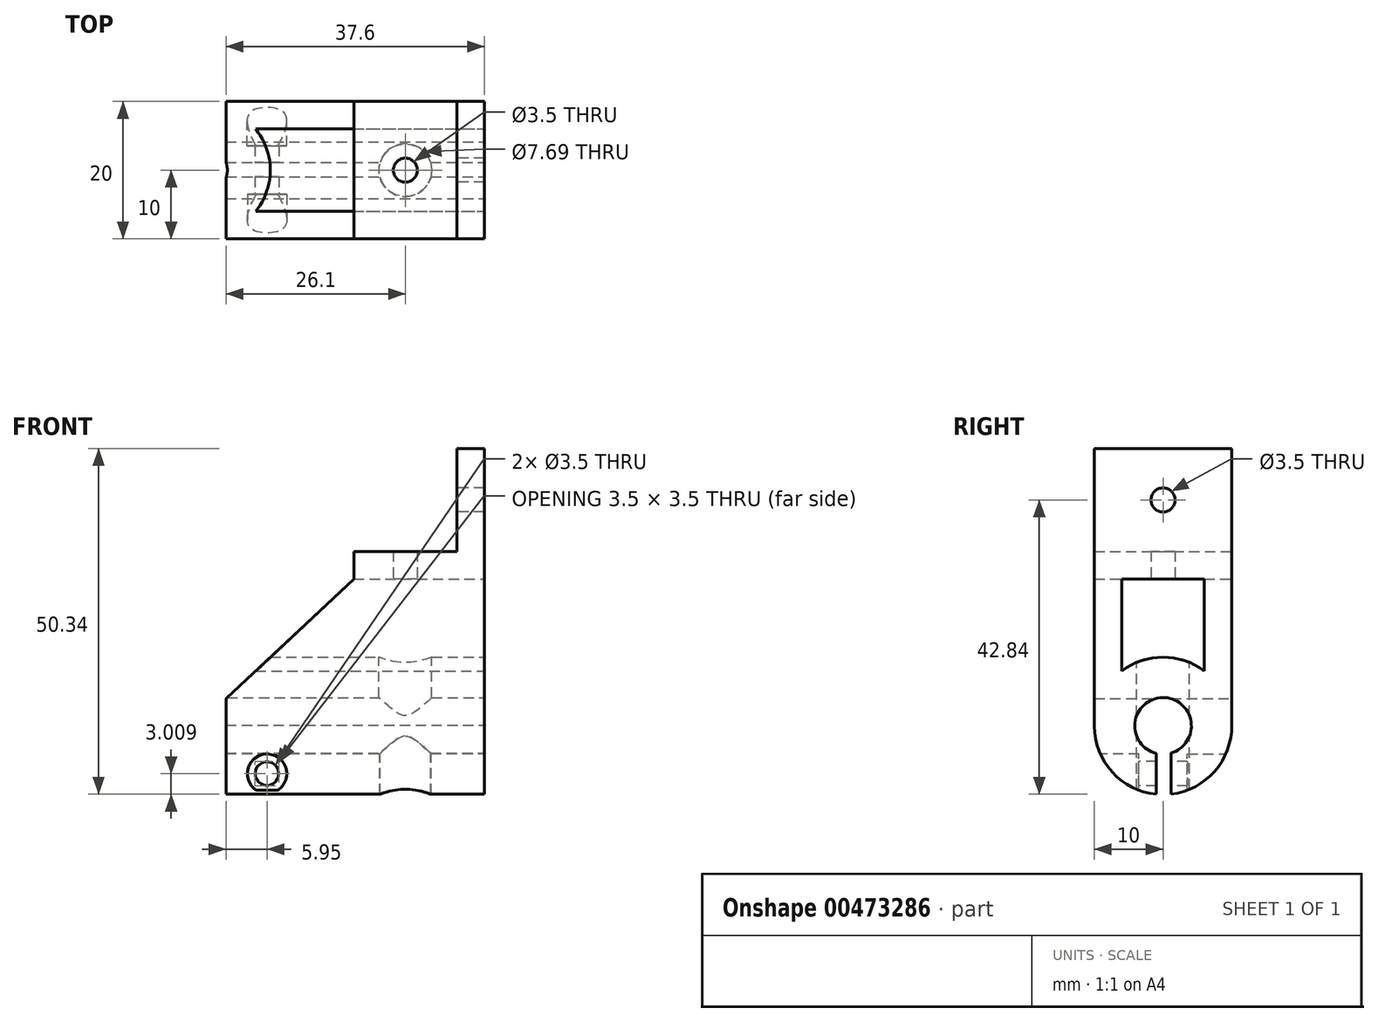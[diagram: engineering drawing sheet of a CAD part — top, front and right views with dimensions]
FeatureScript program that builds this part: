
annotation { "Feature Type Name" : "Feature", "Feature Type Description" : "" }
export const myFeature = defineFeature(function(context is Context, id is Id, definition is map)
    precondition{}
    {
        {
            var Q0;
            Q0=qCreatedBy(makeId("Top.planeOp"),FACE);
            var sketch = newSketch(context, id + "F0", { "sketchPlane" : qUnion([Q0])});
            skLineSegment(sketch, "E0.bottom", {"start": v(0, 0) * mm, "end": v(-19, 0) * mm});
            skLineSegment(sketch, "E0.top", {"start": v(0, 20) * mm, "end": v(-19, 20) * mm});
            skLineSegment(sketch, "E0.left", {"start": v(0, 0) * mm, "end": v(0, 20) * mm});
            skLineSegment(sketch, "E0.right", {"start": v(-19, 0) * mm, "end": v(-19, 20) * mm});
            skPoint(sketch, "E1.centerSnap0", {"position": v(-9.5, 20) * mm});
            skPoint(sketch, "E1.centerSnap1", {"position": v(-19, 10) * mm});
            skCircle(sketch, "E2", {"center": v(-11.5, 10) * mm, "radius": 1.75 * mm});
            skSolve(sketch);
        }
        {
            var Q0;
            Q0 = qSketchRegion(id + "F0", true);
            extrude(context, id + "F1", {"entities" : qUnion([Q0]), "depth" : 4 * mm, "offsetDistance" : 25 * mm});
        }
        {
            var Q0;
            Q0=makeQuery(id+"F1.opExtrude","CAP_FACE",FACE,{"disambiguationData":[OSD([sQuery(id+"F0.wireOp",EDGE,"E0.bottom"),sQuery(id+"F0.wireOp",EDGE,"E0.top"),sQuery(id+"F0.wireOp",EDGE,"E0.left"),sQuery(id+"F0.wireOp",EDGE,"E0.right"),sQuery(id+"F0.wireOp",EDGE,"E1")])],"isStart":false});
            var sketch = newSketch(context, id + "F2", { "sketchPlane" : qUnion([Q0])});
            skSolve(sketch);
        }
        {
            var Q0;
            Q0=makeQuery(id+"F2.imprint","IMPRINT",FACE,{"disambiguationData":[TD([[makeQuery(id+"F2.imprint","IMPRINT",EDGE,{"derivedFrom":makeQuery(id+"F1.opExtrude","CAP_EDGE",EDGE,{"disambiguationData":[OSD([sQuery(id+"F0.wireOp",EDGE,"E0.bottom")])],"isStart":false})}),-1.0]])]});
            var sketch = newSketch(context, id + "F3", { "sketchPlane" : qUnion([Q0])});
            skPoint(sketch, "E3.0", {"position": v(0, 20) * mm});
            skLineSegment(sketch, "E4.bottom", {"start": v(0, 0) * mm, "end": v(-4, 0) * mm});
            skLineSegment(sketch, "E4.top", {"start": v(0, 20) * mm, "end": v(-4, 20) * mm});
            skLineSegment(sketch, "E4.left", {"start": v(0, 0) * mm, "end": v(0, 20) * mm});
            skLineSegment(sketch, "E4.right", {"start": v(-4, 0) * mm, "end": v(-4, 20) * mm});
            skSolve(sketch);
        }
        {
            var Q0;
            Q0 = qSketchRegion(id + "F3", true);
            extrude(context, id + "F4", {"entities" : qUnion([Q0]), "operationType" : NewBodyOperationType.ADD, "depth" : 15 * mm, "offsetDistance" : 25 * mm});
        }
        {
            var Q0;
            Q0=makeQuery(id+"F4.opExtrude","SWEPT_FACE",FACE,{"disambiguationData":[OSD([sQuery(id+"F3.wireOp",EDGE,"E4.right")])]});
            var sketch = newSketch(context, id + "F5", { "sketchPlane" : qUnion([Q0])});
            skCircle(sketch, "E5", {"center": v(-10, 11.5) * mm, "radius": 1.75 * mm});
            skPoint(sketch, "E5.centerSnap0", {"position": v(-20, 11.5) * mm});
            skPoint(sketch, "E5.centerSnap1", {"position": v(-10, 19) * mm});
            skSolve(sketch);
        }
        {
            var Q0;
            Q0 = qSketchRegion(id + "F5", true);
            extrude(context, id + "F6", {"entities" : qUnion([Q0]), "operationType" : NewBodyOperationType.REMOVE, "oppositeDirection" : true, "depth" : 25 * mm, "offsetDistance" : 25 * mm});
        }
        {
            var Q0;
            Q0=makeQuery(id+"F4.boolean.opBoolean","MERGE",FACE,{"derivedFrom":[makeQuery(id+"F1.opExtrude","SWEPT_FACE",FACE,{"disambiguationData":[OSD([sQuery(id+"F0.wireOp",EDGE,"E0.left")])]}),makeQuery(id+"F4.opExtrude","SWEPT_FACE",FACE,{"disambiguationData":[OSD([sQuery(id+"F3.wireOp",EDGE,"E4.left")])]})]});
            var sketch = newSketch(context, id + "F7", { "sketchPlane" : qUnion([Q0])});
            skLineSegment(sketch, "E6.bottom", {"start": v(0, 0) * mm, "end": v(4, 0) * mm});
            skLineSegment(sketch, "E6.left", {"start": v(0, 0) * mm, "end": v(0, -21.38) * mm});
            skLineSegment(sketch, "E6.right", {"start": v(4, 0) * mm, "end": v(4, -13.38) * mm});
            skLineSegment(sketch, "E7.bottom", {"start": v(20, 0) * mm, "end": v(16, 0) * mm});
            skLineSegment(sketch, "E7.left", {"start": v(20, 0) * mm, "end": v(20, -21.26) * mm});
            skLineSegment(sketch, "E7.right", {"start": v(16, 0) * mm, "end": v(16, -13.38) * mm});
            skArc(sketch, "E8", {"start": v(0, -21.38) * mm, "mid": v(10.06, -31.39) * mm, "end": v(20, -21.26) * mm});
            skPoint(sketch, "E8.centerSnap0", {"position": v(10, 0) * mm});
            skCircle(sketch, "E9", {"center": v(10, -21.38) * mm, "radius": 4.12 * mm});
            skPoint(sketch, "E6.top.end.orphan", {"position": v(4, -21.38) * mm});
            skArc(sketch, "E10.trimOffspring", {"start": v(16, -13.38) * mm, "mid": v(10, -11.38) * mm, "end": v(4, -13.38) * mm});
            skSolve(sketch);
        }
        {
            var Q0;
            Q0 = qSketchRegion(id + "F7", true);
            extrude(context, id + "F8", {"entities" : qUnion([Q0]), "operationType" : NewBodyOperationType.ADD, "oppositeDirection" : true, "depth" : 37.6 * mm, "offsetDistance" : 25 * mm});
        }
        {
            var Q0;
            Q0=makeQuery(id+"F1.opExtrude","CAP_FACE",FACE,{"disambiguationData":[OSD([sQuery(id+"F0.wireOp",EDGE,"E0.bottom"),sQuery(id+"F0.wireOp",EDGE,"E0.top"),sQuery(id+"F0.wireOp",EDGE,"E0.left"),sQuery(id+"F0.wireOp",EDGE,"E0.right"),sQuery(id+"F0.wireOp",EDGE,"E2")])],"isStart":true});
            var sketch = newSketch(context, id + "F9", { "sketchPlane" : qUnion([Q0])});
            skCircle(sketch, "E11", {"center": v(-11.5, -10) * mm, "radius": 3.85 * mm});
            skSolve(sketch);
        }
        {
            var Q0;
            Q0 = qSketchRegion(id + "F9", true);
            extrude(context, id + "F10", {"entities" : qUnion([Q0]), "operationType" : NewBodyOperationType.REMOVE, "depth" : 43.1 * mm, "offsetDistance" : 25 * mm});
        }
        {
            var Q0;
            Q0=makeQuery(id+"F8.opExtrude","SWEPT_FACE",FACE,{"disambiguationData":[OSD([sQuery(id+"F7.wireOp",EDGE,"E7.left")])]});
            var sketch = newSketch(context, id + "F11", { "sketchPlane" : qUnion([Q0])});
            skLineSegment(sketch, "E12", {"start": v(19, 0) * mm, "end": v(37.6, -17.43) * mm});
            skLineSegment(sketch, "E13", {"start": v(37.6, -17.43) * mm, "end": v(41.8, 4.6) * mm});
            skLineSegment(sketch, "E14", {"start": v(41.8, 4.6) * mm, "end": v(19.61, 0) * mm});
            skLineSegment(sketch, "E15", {"start": v(19.61, 0) * mm, "end": v(19, 0) * mm});
            skSolve(sketch);
        }
        {
            var Q0;
            Q0 = qSketchRegion(id + "F11", true);
            extrude(context, id + "F12", {"entities" : qUnion([Q0]), "operationType" : NewBodyOperationType.REMOVE, "oppositeDirection" : true, "depth" : 25 * mm, "offsetDistance" : 25 * mm});
        }
        {
            var Q0;
            Q0=makeQuery(id+"F8.boolean.opBoolean","MERGE",FACE,{"derivedFrom":[makeQuery(id+"F4.boolean.opBoolean","MERGE",FACE,{"derivedFrom":[makeQuery(id+"F1.opExtrude","SWEPT_FACE",FACE,{"disambiguationData":[OSD([sQuery(id+"F0.wireOp",EDGE,"E0.left")])]}),makeQuery(id+"F4.opExtrude","SWEPT_FACE",FACE,{"disambiguationData":[OSD([sQuery(id+"F3.wireOp",EDGE,"E4.left")])]})]}),makeQuery(id+"F8.opExtrude","CAP_FACE",FACE,{"disambiguationData":[OSD([sQuery(id+"F7.wireOp",EDGE,"E6.bottom"),sQuery(id+"F7.wireOp",EDGE,"E6.left"),sQuery(id+"F7.wireOp",EDGE,"E6.right"),sQuery(id+"F7.wireOp",EDGE,"E7.bottom"),sQuery(id+"F7.wireOp",EDGE,"E7.left"),sQuery(id+"F7.wireOp",EDGE,"E7.right"),sQuery(id+"F7.wireOp",EDGE,"E8"),sQuery(id+"F7.wireOp",EDGE,"E9"),sQuery(id+"F7.wireOp",EDGE,"E10.trimOffspring")])],"isStart":true})]});
            var sketch = newSketch(context, id + "F13", { "sketchPlane" : qUnion([Q0])});
            skLineSegment(sketch, "E16.bottom", {"start": v(9.04, -21.3) * mm, "end": v(11.16, -21.3) * mm});
            skLineSegment(sketch, "E16.top", {"start": v(9.04, -33.47) * mm, "end": v(11.16, -33.47) * mm});
            skLineSegment(sketch, "E16.left", {"start": v(9.04, -21.3) * mm, "end": v(9.04, -33.47) * mm});
            skLineSegment(sketch, "E16.right", {"start": v(11.16, -21.3) * mm, "end": v(11.16, -33.47) * mm});
            skSolve(sketch);
        }
        {
            var Q0;
            Q0 = qSketchRegion(id + "F13", true);
            extrude(context, id + "F14", {"entities" : qUnion([Q0]), "operationType" : NewBodyOperationType.REMOVE, "oppositeDirection" : true, "depth" : 49.3 * mm, "offsetDistance" : 25 * mm});
        }
        {
            var Q0;
            {var subQ0=sQuery(id+"F7.wireOp",EDGE,"E9");var subQ1=sQuery(id+"F7.wireOp",EDGE,"E8");Q0=makeQuery(id+"F14.boolean.opBoolean","COPY",FACE,{"disambiguationData":[TD([makeQuery(id+"F8.opExtrude","CAP_FACE",FACE,{"disambiguationData":[OSD([sQuery(id+"F7.wireOp",EDGE,"E6.bottom"),sQuery(id+"F7.wireOp",EDGE,"E6.left"),sQuery(id+"F7.wireOp",EDGE,"E6.right"),sQuery(id+"F7.wireOp",EDGE,"E7.bottom"),sQuery(id+"F7.wireOp",EDGE,"E7.left"),sQuery(id+"F7.wireOp",EDGE,"E7.right"),subQ1,subQ0,sQuery(id+"F7.wireOp",EDGE,"E10.trimOffspring")])],"isStart":false})])],"derivedFrom":makeQuery(id+"F14.opExtrude","SWEPT_FACE",FACE,{"disambiguationData":[OSD([sQuery(id+"F13.wireOp",EDGE,"E16.right")])]})});}
            var sketch = newSketch(context, id + "F15", { "sketchPlane" : qUnion([Q0])});
            skCircle(sketch, "E17", {"center": v(-31.65, -28.33) * mm, "radius": 1.75 * mm});
            skPoint(sketch, "E17.centerSnap0", {"position": v(-37.6, -28.33) * mm});
            skSolve(sketch);
        }
        {
            var Q0;
            Q0 = qSketchRegion(id + "F15", true);
            extrude(context, id + "F16", {"entities" : qUnion([Q0]), "operationType" : NewBodyOperationType.REMOVE, "oppositeDirection" : true, "depth" : 25 * mm, "offsetDistance" : 25 * mm, "hasSecondDirection" : true, "secondDirectionOppositeDirection" : false, "secondDirectionDepth" : 25 * mm});
        }
        {
            var Q0;
            Q0=makeQuery(id+"F8.opExtrude","SWEPT_FACE",FACE,{"disambiguationData":[OSD([sQuery(id+"F7.wireOp",EDGE,"E6.left")])]});
            var sketch = newSketch(context, id + "F17", { "sketchPlane" : qUnion([Q0])});
            skFitSpline(sketch, "E18.0", {"points": [v(-32.07, -30.04) * mm, v(-31.65, -30.1) * mm, v(-31.23, -30.04) * mm, v(-30.88, -29.92) * mm, v(-30.6, -29.74) * mm, v(-30.37, -29.54) * mm, v(-30.2, -29.32) * mm, v(-30, -28.98) * mm, v(-29.88, -28.52) * mm, v(-29.91, -27.9) * mm, v(-30.15, -27.37) * mm, v(-30.46, -27.04) * mm, v(-30.66, -26.88) * mm, v(-30.9, -26.74) * mm, v(-31.15, -26.64) * mm, v(-31.43, -26.6) * mm, v(-31.71, -26.57) * mm, v(-32.07, -26.61) * mm, v(-32.46, -26.76) * mm, v(-32.8, -26.99) * mm, v(-33.14, -27.36) * mm, v(-33.39, -27.9) * mm, v(-33.42, -28.41) * mm, v(-33.34, -28.8) * mm, v(-33.25, -29.06) * mm, v(-33.1, -29.31) * mm, v(-32.92, -29.54) * mm, v(-32.7, -29.74) * mm, v(-32.42, -29.92) * mm, v(-32.07, -30.04) * mm, v(-31.65, -30.1) * mm, v(-31.23, -30.04) * mm, v(-32.07, -30.04) * mm]});
            skCircle(sketch, "E19", {"center": v(-31.64, -28.34) * mm, "radius": 2.87 * mm});
            skSolve(sketch);
        }
        {
            var Q0;
            Q0 = qSketchRegion(id + "F17", true);
            extrude(context, id + "F18", {"entities" : qUnion([Q0]), "operationType" : NewBodyOperationType.REMOVE, "oppositeDirection" : true, "depth" : 6.5 * mm, "offsetDistance" : 25 * mm});
        }
        {
            var Q0;
            Q0=makeQuery(id+"F8.opExtrude","SWEPT_FACE",FACE,{"disambiguationData":[OSD([sQuery(id+"F7.wireOp",EDGE,"E7.left")])]});
            var sketch = newSketch(context, id + "F19", { "sketchPlane" : qUnion([Q0])});
            skFitSpline(sketch, "E20.0", {"points": [v(30.1, -30.75) * mm, v(29.9, -30.63) * mm, v(29.55, -30.34) * mm, v(29.13, -29.78) * mm, v(28.88, -29.2) * mm, v(28.78, -28.66) * mm, v(28.77, -28.23) * mm, v(28.82, -27.78) * mm, v(28.95, -27.3) * mm, v(29.14, -26.92) * mm, v(29.34, -26.62) * mm, v(29.58, -26.33) * mm, v(29.93, -26.02) * mm, v(30.36, -25.76) * mm, v(30.73, -25.62) * mm, v(31.02, -25.54) * mm, v(31.33, -25.49) * mm, v(31.73, -25.46) * mm, v(32.14, -25.5) * mm, v(32.53, -25.6) * mm, v(32.81, -25.72) * mm, v(33.08, -25.85) * mm, v(33.4, -26.06) * mm, v(33.7, -26.32) * mm, v(33.93, -26.6) * mm, v(34.14, -26.9) * mm, v(34.33, -27.3) * mm, v(34.46, -27.77) * mm, v(34.54, -28.37) * mm, v(34.45, -29.07) * mm, v(34.16, -29.77) * mm, v(33.74, -30.34) * mm, v(33.39, -30.63) * mm, v(33.2, -30.75) * mm]});
            skLineSegment(sketch, "E21", {"start": v(33.2, -30.75) * mm, "end": v(30.1, -30.75) * mm});
            skSolve(sketch);
        }
        {
            var Q0;
            Q0 = qSketchRegion(id + "F19", true);
            extrude(context, id + "F20", {"entities" : qUnion([Q0]), "operationType" : NewBodyOperationType.REMOVE, "oppositeDirection" : true, "depth" : 6.47 * mm, "offsetDistance" : 25 * mm});
        }
    });
